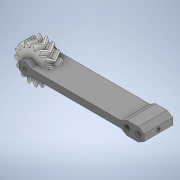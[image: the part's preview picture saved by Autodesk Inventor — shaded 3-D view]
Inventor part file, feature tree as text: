
AUTODESK INVENTOR PART (.ipt)
format: ipt  version: 2020 (Build 240168000, 168)  size: 982,016 bytes
history: native  units: in
note: dims shown in document units (in); Inventor stores cm internally (conversion verified against a paired STEP export)
features: sketch x5, extrude x4, other x3, plane x2, mirror x1, projected_geometry x1
ambient origin geometry x8: Origin, YZ Plane, XZ Plane, XY Plane, X Axis, Y Axis, Z Axis, Center Point
bodies: Solid1 (feature_tree), Solid2 (feature_tree)
feature tree (16):
  other  "Spur Gear1"
  plane  "Work Plane3"
  extrude  "Extrusion1"  Depth=3.4256in
  plane  "Work Plane1"
  extrude  "Extrusion2"  Depth=0.7874in
  sketch  "Sketch4"  dims[d4=0.0in d5=0.0906in]
  extrude  "Extrusion4"  Depth=0.0906in
  mirror  "Mirror3"
  extrude  "Extrusion11"  Depth=0.315in
  sketch  "Sketch1"  dims[d0=0.1818in d1=3.4256in]
  sketch  "Sketch2"  dims[d2=0.0945in d3=0.7874in]
  sketch  "Sketch5"  dims[d6=0.7874in d7=0.0in d29=0.315in]
  other  "Solid1::Spur Gear1"
  other  "TaggingFeature1"
  projected_geometry  "Projected Loop11"
  sketch  "Sketch15"  dims[d31=0.315in d33=0.1476in d34=0.2362in d35=0.0in d38=0.315in d69=2.4807in d70=0.3937in d71=0.1969in d79=0.0in d80=0.3937in d81=0.0in]
